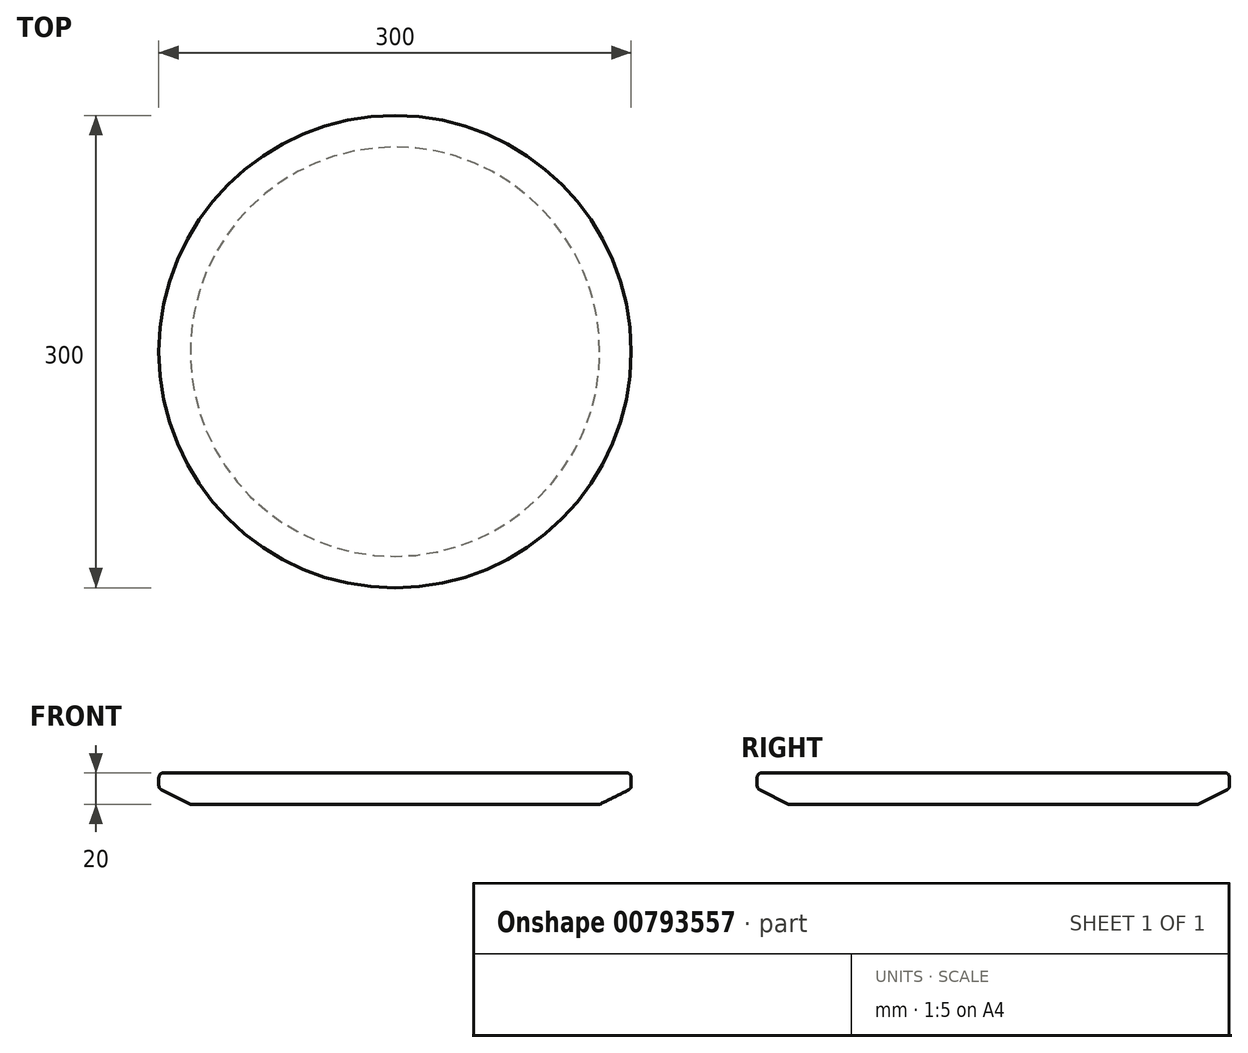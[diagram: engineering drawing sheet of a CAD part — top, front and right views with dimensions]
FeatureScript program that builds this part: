
annotation { "Feature Type Name" : "Feature", "Feature Type Description" : "" }
export const myFeature = defineFeature(function(context is Context, id is Id, definition is map)
    precondition{}
    {
        {
            var Q0;
            Q0=qCreatedBy(makeId("Top.planeOp"),FACE);
            var sketch = newSketch(context, id + "F0", { "sketchPlane" : qUnion([Q0])});
            skCircle(sketch, "E0", {"center": v(0, 0) * mm, "radius": 150 * mm});
            skSolve(sketch);
        }
        {
            var Q0;
            Q0 = qSketchRegion(id + "F0", true);
            extrude(context, id + "F1", {"entities" : qUnion([Q0]), "depth" : 20 * mm, "offsetDistance" : 25 * mm});
        }
        {
            var Q0;
            Q0=makeQuery(id+"F1.opExtrude","CAP_FACE",FACE,{"disambiguationData":[OSD([sQuery(id+"F0.wireOp",EDGE,"E0")])],"isStart":true});
            chamfer(context, id + "F2", {"entities" : qUnion([Q0]), "chamferType" : ChamferType.TWO_OFFSETS, "width1" : 10 * mm, "oppositeDirection" : false, "width2" : 20 * mm, "tangentPropagation" : true});
        }
        {
            var Q0;
            Q0=makeQuery(id+"F1.opExtrude","CAP_EDGE",EDGE,{"disambiguationData":[OSD([sQuery(id+"F0.wireOp",EDGE,"E0")])],"isStart":false});
            fillet(context, id + "F3", {"entities" : qUnion([Q0]), "radius" : 3 * mm, "tangentPropagation" : true, "allowEdgeOverflow" : false});
        }
        {
            var Q0;
            {var subQ0=sQuery(id+"F0.wireOp",EDGE,"E0");Q0=makeQuery(id+"F2.opChamfer","BLEND_EDGE",EDGE,{"blendedFrom":[makeQuery(id+"F1.opExtrude","CAP_EDGE",EDGE,{"disambiguationData":[OSD([subQ0])],"isStart":true}),makeQuery(id+"F1.opExtrude","SWEPT_FACE",FACE,{"disambiguationData":[OSD([subQ0])]})],"blendedInto":[makeQuery(id+"F1.opExtrude","SWEPT_FACE",FACE,{"disambiguationData":[OSD([subQ0])]})]});}
            fillet(context, id + "F4", {"entities" : qUnion([Q0]), "radius" : 3 * mm, "tangentPropagation" : true, "allowEdgeOverflow" : false});
        }
    });
